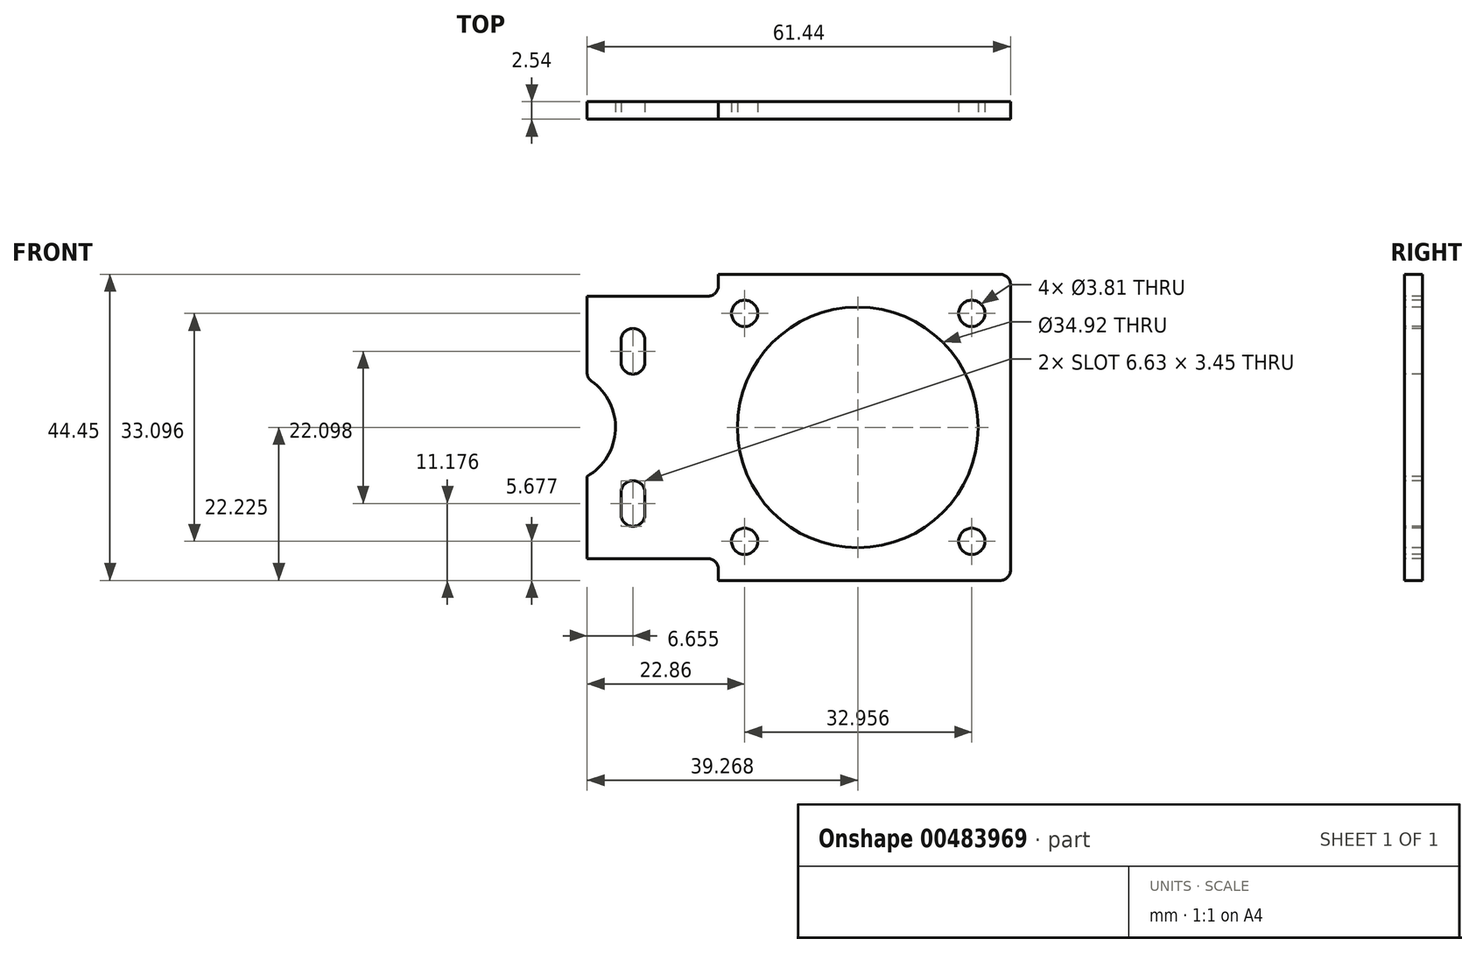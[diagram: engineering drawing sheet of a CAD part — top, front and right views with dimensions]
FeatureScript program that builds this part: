
annotation { "Feature Type Name" : "Feature", "Feature Type Description" : "" }
export const myFeature = defineFeature(function(context is Context, id is Id, definition is map)
    precondition{}
    {
        {
            var Q0;
            Q0=qCreatedBy(makeId("Top.planeOp"),FACE);
            var sketch = newSketch(context, id + "F0", { "sketchPlane" : qUnion([Q0])});
            skLineSegment(sketch, "E0.bottom", {"start": v(0, 0) * mm, "end": v(-30.48, 0) * mm});
            skLineSegment(sketch, "E0.top", {"start": v(0, 2.54) * mm, "end": v(-30.48, 2.54) * mm});
            skLineSegment(sketch, "E0.left", {"start": v(0, 0) * mm, "end": v(0, 2.54) * mm});
            skLineSegment(sketch, "E0.right", {"start": v(-30.48, 0) * mm, "end": v(-30.48, 2.54) * mm});
            skLineSegment(sketch, "E1", {"start": v(0, 2.54) * mm, "end": v(30.96, 2.54) * mm});
            skLineSegment(sketch, "E2", {"start": v(30.96, 2.54) * mm, "end": v(30.96, 0) * mm});
            skLineSegment(sketch, "E3", {"start": v(30.96, 0) * mm, "end": v(0, 0) * mm});
            skSolve(sketch);
        }
        {
            var Q0;
            Q0=makeQuery(id+"F0.imprint","IMPRINT",FACE,{"disambiguationData":[TD([[makeQuery(id+"F0.imprint","IMPRINT",EDGE,{"derivedFrom":sQuery(id+"F0.wireOp",EDGE,"E0.bottom")}),-1.0]])]});
            extrude(context, id + "F1", {"entities" : qUnion([Q0]), "depth" : 44.45 * mm});
        }
        {
            var Q0;
            Q0=makeQuery(id+"F1.opExtrude","SWEPT_FACE",FACE,{"disambiguationData":[OSD([sQuery(id+"F0.wireOp",EDGE,"E0.bottom")])]});
            var sketch = newSketch(context, id + "F2", { "sketchPlane" : qUnion([Q0])});
            skLineSegment(sketch, "E4", {"start": v(-30.48, 22.23) * mm, "end": v(-26.37, 22.23) * mm, "construction": true});
            skPoint(sketch, "E5", {"position": v(-30.48, 29.34) * mm});
            skPoint(sketch, "E6", {"position": v(-30.48, 15.11) * mm});
            skArc(sketch, "E7", {"start": v(-30.48, 15.11) * mm, "mid": v(-26.37, 22.23) * mm, "end": v(-30.48, 29.34) * mm});
            skLineSegment(sketch, "E8", {"start": v(-26.37, 22.23) * mm, "end": v(-23.83, 22.23) * mm, "construction": true});
            skLineSegment(sketch, "E9", {"start": v(-23.83, 33.27) * mm, "end": v(-23.83, 12.76) * mm, "construction": true});
            skLineSegment(sketch, "E10", {"start": v(-23.83, 33.27) * mm, "end": v(-23.83, 34.86) * mm, "construction": true});
            skLineSegment(sketch, "E11", {"start": v(-23.83, 11.18) * mm, "end": v(-23.83, 9.59) * mm, "construction": true});
            skLineSegment(sketch, "E12", {"start": v(-23.83, 33.27) * mm, "end": v(-23.83, 31.69) * mm, "construction": true});
            skArc(sketch, "E13", {"start": v(-22.1, 34.86) * mm, "mid": v(-23.83, 36.59) * mm, "end": v(-25.55, 34.86) * mm});
            skArc(sketch, "E14", {"start": v(-25.55, 31.69) * mm, "mid": v(-23.83, 29.96) * mm, "end": v(-22.1, 31.69) * mm});
            skArc(sketch, "E15", {"start": v(-22.1, 12.76) * mm, "mid": v(-23.83, 14.5) * mm, "end": v(-25.55, 12.76) * mm});
            skArc(sketch, "E16", {"start": v(-25.55, 9.59) * mm, "mid": v(-23.83, 7.86) * mm, "end": v(-22.1, 9.59) * mm});
            skLineSegment(sketch, "E17", {"start": v(-25.55, 12.76) * mm, "end": v(-25.55, 9.59) * mm});
            skLineSegment(sketch, "E18", {"start": v(-22.1, 12.76) * mm, "end": v(-22.1, 9.59) * mm});
            skLineSegment(sketch, "E19", {"start": v(-25.55, 34.86) * mm, "end": v(-25.55, 31.69) * mm});
            skLineSegment(sketch, "E20", {"start": v(-22.1, 34.86) * mm, "end": v(-22.1, 31.69) * mm});
            skLineSegment(sketch, "E21.trimOffspring", {"start": v(-23.83, 11.18) * mm, "end": v(-23.83, 12.76) * mm, "construction": true});
            skLineSegment(sketch, "E22.bottom", {"start": v(-30.48, 3.17) * mm, "end": v(-11.43, 3.17) * mm});
            skLineSegment(sketch, "E22.top", {"start": v(-30.48, 0) * mm, "end": v(-11.43, 0) * mm});
            skLineSegment(sketch, "E22.left", {"start": v(-30.48, 3.17) * mm, "end": v(-30.48, 0) * mm});
            skLineSegment(sketch, "E22.right", {"start": v(-11.43, 3.17) * mm, "end": v(-11.43, 0) * mm});
            skLineSegment(sketch, "E23.bottom", {"start": v(-30.48, 44.45) * mm, "end": v(-11.43, 44.45) * mm});
            skLineSegment(sketch, "E23.top", {"start": v(-30.48, 41.28) * mm, "end": v(-11.43, 41.28) * mm});
            skLineSegment(sketch, "E23.left", {"start": v(-30.48, 44.45) * mm, "end": v(-30.48, 41.28) * mm});
            skLineSegment(sketch, "E23.right", {"start": v(-11.43, 44.45) * mm, "end": v(-11.43, 41.28) * mm});
            skLineSegment(sketch, "E24", {"start": v(-11.43, 41.28) * mm, "end": v(-11.43, 3.17) * mm, "construction": true});
            skSolve(sketch);
        }
        {
            var Q0;
            Q0=makeQuery(id+"F0.imprint","IMPRINT",FACE,{"disambiguationData":[TD([[makeQuery(id+"F0.imprint","IMPRINT",EDGE,{"derivedFrom":sQuery(id+"F0.wireOp",EDGE,"E0.left")}),-1.0]])]});
            extrude(context, id + "F3", {"entities" : qUnion([Q0]), "operationType" : NewBodyOperationType.ADD, "depth" : 44.45 * mm});
        }
        {
            var Q0;
            Q0=makeQuery(id+"F3.boolean.opBoolean","MERGE",FACE,{"derivedFrom":[makeQuery(id+"F1.opExtrude","SWEPT_FACE",FACE,{"disambiguationData":[OSD([sQuery(id+"F0.wireOp",EDGE,"E0.bottom")])]}),makeQuery(id+"F3.opExtrude","SWEPT_FACE",FACE,{"disambiguationData":[OSD([sQuery(id+"F0.wireOp",EDGE,"E3")])]})]});
            var sketch = newSketch(context, id + "F4", { "sketchPlane" : qUnion([Q0])});
            skCircle(sketch, "E25", {"center": v(-7.62, 38.77) * mm, "radius": 1.9 * mm});
            skCircle(sketch, "E26", {"center": v(-7.62, 5.68) * mm, "radius": 1.9 * mm});
            skPoint(sketch, "E27", {"position": v(30.96, 5.68) * mm});
            skPoint(sketch, "E28", {"position": v(30.96, 38.77) * mm});
            skPoint(sketch, "E29", {"position": v(0, 22.23) * mm});
            skLineSegment(sketch, "E30", {"start": v(0, 0) * mm, "end": v(0, 44.45) * mm, "construction": true});
            skLineSegment(sketch, "E31", {"start": v(0, 22.23) * mm, "end": v(8.79, 22.23) * mm, "construction": true});
            skPoint(sketch, "E32", {"position": v(30.96, 34.36) * mm});
            skPoint(sketch, "E33", {"position": v(30.96, 5.09) * mm});
            skCircle(sketch, "E34", {"center": v(8.79, 22.23) * mm, "radius": 17.46 * mm});
            skLineSegment(sketch, "E35", {"start": v(-11.79, 44.45) * mm, "end": v(-11.79, 0) * mm, "construction": true});
            skLineSegment(sketch, "E36", {"start": v(-7.62, 38.77) * mm, "end": v(25.34, 38.77) * mm, "construction": true});
            skLineSegment(sketch, "E37", {"start": v(25.34, 38.77) * mm, "end": v(25.34, 5.68) * mm, "construction": true});
            skLineSegment(sketch, "E38", {"start": v(25.34, 5.68) * mm, "end": v(-7.62, 5.68) * mm, "construction": true});
            skLineSegment(sketch, "E39", {"start": v(5.98, 39.69) * mm, "end": v(12.26, 39.69) * mm, "construction": true});
            skLineSegment(sketch, "E40", {"start": v(26.25, 25.32) * mm, "end": v(26.25, 19.37) * mm, "construction": true});
            skCircle(sketch, "E41", {"center": v(25.34, 38.77) * mm, "radius": 1.9 * mm});
            skCircle(sketch, "E42", {"center": v(25.34, 5.68) * mm, "radius": 1.9 * mm});
            skPoint(sketch, "E43", {"position": v(21.92, 0) * mm});
            skSolve(sketch);
        }
        {
            var Q0;
            {var subQ0=sQuery(id+"F4.wireOp",EDGE,"oErodHu0-SVqe-cXD9-A2Iy-klHVv3QFz86o");Q0=makeQuery(id+"F4.imprint","IMPRINT",FACE,{"disambiguationData":[TD([[makeQuery(id+"F4.imprint","IMPRINT",EDGE,{"derivedFrom":subQ0}),1.0]])]});}
            var Q1;
            Q1=makeQuery(id+"F4.imprint","IMPRINT",FACE,{"disambiguationData":[TD([[makeQuery(id+"F4.imprint","IMPRINT",EDGE,{"derivedFrom":sQuery(id+"F4.wireOp",EDGE,"E25")}),1.0]])]});
            var Q2;
            Q2=makeQuery(id+"F4.imprint","IMPRINT",FACE,{"disambiguationData":[TD([[makeQuery(id+"F4.imprint","IMPRINT",EDGE,{"derivedFrom":sQuery(id+"F4.wireOp",EDGE,"E26")}),1.0]])]});
            var Q3;
            Q3=makeQuery(id+"F2.imprint","IMPRINT",FACE,{"disambiguationData":[TD([[makeQuery(id+"F2.imprint","IMPRINT",EDGE,{"derivedFrom":sQuery(id+"F2.wireOp",EDGE,"E15")}),1.0]])]});
            var Q4;
            Q4=makeQuery(id+"F2.imprint","IMPRINT",FACE,{"disambiguationData":[TD([[makeQuery(id+"F2.imprint","IMPRINT",EDGE,{"derivedFrom":sQuery(id+"F2.wireOp",EDGE,"E13")}),1.0]])]});
            var Q5;
            {var subQ0=sQuery(id+"F2.wireOp",EDGE,"E7");Q5=makeQuery(id+"F2.imprint","IMPRINT",FACE,{"disambiguationData":[TD([[makeQuery(id+"F2.imprint","IMPRINT",EDGE,{"derivedFrom":subQ0}),1.0]])]});}
            var Q6;
            {var subQ0=sQuery(id+"F4.wireOp",EDGE,"mWe7BF5G-u2iA-ggOj-CAzd-YLydOq5GdBwD");Q6=makeQuery(id+"F4.imprint","IMPRINT",FACE,{"disambiguationData":[TD([[makeQuery(id+"F4.imprint","IMPRINT",EDGE,{"derivedFrom":subQ0}),1.0]])]});}
            var Q7;
            Q7=makeQuery(id+"F4.imprint","IMPRINT",FACE,{"disambiguationData":[TD([[makeQuery(id+"F4.imprint","IMPRINT",EDGE,{"derivedFrom":sQuery(id+"F4.wireOp",EDGE,"E41")}),1.0]])]});
            var Q8;
            Q8=makeQuery(id+"F4.imprint","IMPRINT",FACE,{"disambiguationData":[TD([[makeQuery(id+"F4.imprint","IMPRINT",EDGE,{"derivedFrom":sQuery(id+"F4.wireOp",EDGE,"E42")}),1.0]])]});
            var Q9;
            Q9=makeQuery(id+"F4.imprint","IMPRINT",FACE,{"disambiguationData":[TD([[makeQuery(id+"F4.imprint","IMPRINT",EDGE,{"derivedFrom":sQuery(id+"F4.wireOp",EDGE,"E34")}),1.0]])]});
            extrude(context, id + "F5", {"entities" : qUnion([Q0, Q1, Q2, Q3, Q4, Q5, Q6, Q7, Q8, Q9]), "operationType" : NewBodyOperationType.REMOVE, "oppositeDirection" : true, "depth" : 25.4 * mm});
        }
        {
            var Q0;
            Q0=makeQuery(id+"F2.imprint","IMPRINT",FACE,{"disambiguationData":[TD([[makeQuery(id+"F2.imprint","IMPRINT",EDGE,{"derivedFrom":sQuery(id+"F2.wireOp",EDGE,"E23.bottom")}),1.0]])]});
            var Q1;
            Q1=makeQuery(id+"F2.imprint","IMPRINT",FACE,{"disambiguationData":[TD([[makeQuery(id+"F2.imprint","IMPRINT",EDGE,{"derivedFrom":sQuery(id+"F2.wireOp",EDGE,"E22.bottom")}),-1.0]])]});
            extrude(context, id + "F6", {"entities" : qUnion([Q0, Q1]), "operationType" : NewBodyOperationType.REMOVE, "oppositeDirection" : true, "depth" : 25.4 * mm});
        }
        {
            var Q0;
            Q0=makeQuery(id+"F6.boolean.opBoolean","COPY",EDGE,{"derivedFrom":makeQuery(id+"F6.opExtrude","SWEPT_EDGE",EDGE,{"disambiguationData":[OSD([sQuery(id+"F2.wireOp",EDGE,"E23.top"),sQuery(id+"F2.wireOp",EDGE,"E23.right")])]})});
            var Q1;
            Q1=makeQuery(id+"F6.boolean.opBoolean","COPY",EDGE,{"derivedFrom":makeQuery(id+"F6.opExtrude","SWEPT_EDGE",EDGE,{"disambiguationData":[OSD([sQuery(id+"F0.wireOp",EDGE,"E0.bottom"),sQuery(id+"F2.wireOp",EDGE,"E23.bottom"),sQuery(id+"F2.wireOp",EDGE,"E23.right")])]})});
            var Q2;
            Q2=makeQuery(id+"F6.boolean.opBoolean","COPY",EDGE,{"derivedFrom":makeQuery(id+"F6.opExtrude","SWEPT_EDGE",EDGE,{"disambiguationData":[OSD([sQuery(id+"F0.wireOp",EDGE,"E0.bottom"),sQuery(id+"F2.wireOp",EDGE,"E22.top"),sQuery(id+"F2.wireOp",EDGE,"E22.right")])]})});
            var Q3;
            Q3=makeQuery(id+"F6.boolean.opBoolean","COPY",EDGE,{"derivedFrom":makeQuery(id+"F6.opExtrude","SWEPT_EDGE",EDGE,{"disambiguationData":[OSD([sQuery(id+"F2.wireOp",EDGE,"E22.bottom"),sQuery(id+"F2.wireOp",EDGE,"E22.right")])]})});
            var Q4;
            Q4=makeQuery(id+"F6.boolean.opBoolean","COPY",EDGE,{"derivedFrom":makeQuery(id+"F6.opExtrude","SWEPT_EDGE",EDGE,{"disambiguationData":[OSD([sQuery(id+"F0.wireOp",EDGE,"E0.bottom"),sQuery(id+"F0.wireOp",EDGE,"E0.right"),sQuery(id+"F2.wireOp",EDGE,"E22.bottom"),sQuery(id+"F2.wireOp",EDGE,"E22.left")])]})});
            var Q5;
            {var subQ0=sQuery(id+"F2.wireOp",EDGE,"E7");var subQ1=sQuery(id+"F0.wireOp",EDGE,"E0.right");var subQ2=sQuery(id+"F0.wireOp",EDGE,"E0.bottom");Q5=makeQuery(id+"F5.boolean.opBoolean","COPY",EDGE,{"derivedFrom":makeQuery(id+"F5.opExtrude","SWEPT_EDGE",EDGE,{"disambiguationData":[OSD([subQ2,subQ1,subQ0]),TDD([makeQuery(id+"F2.imprint","INTERSECT",VERTEX,{"disambiguationData":[OD(0.0)],"derivedFrom":[makeQuery(id+"F1.opExtrude","SWEPT_EDGE",EDGE,{"disambiguationData":[OSD([subQ2,subQ1])]}),subQ0]})])]})});}
            var Q6;
            {var subQ0=sQuery(id+"F2.wireOp",EDGE,"E7");var subQ1=sQuery(id+"F0.wireOp",EDGE,"E0.right");var subQ2=sQuery(id+"F0.wireOp",EDGE,"E0.bottom");Q6=makeQuery(id+"F5.boolean.opBoolean","COPY",EDGE,{"derivedFrom":makeQuery(id+"F5.opExtrude","SWEPT_EDGE",EDGE,{"disambiguationData":[OSD([subQ2,subQ1,subQ0]),TDD([makeQuery(id+"F2.imprint","INTERSECT",VERTEX,{"disambiguationData":[OD(1.0)],"derivedFrom":[makeQuery(id+"F1.opExtrude","SWEPT_EDGE",EDGE,{"disambiguationData":[OSD([subQ2,subQ1])]}),subQ0]})])]})});}
            var Q7;
            Q7=makeQuery(id+"F6.boolean.opBoolean","COPY",EDGE,{"derivedFrom":makeQuery(id+"F6.opExtrude","SWEPT_EDGE",EDGE,{"disambiguationData":[OSD([sQuery(id+"F0.wireOp",EDGE,"E0.bottom"),sQuery(id+"F0.wireOp",EDGE,"E0.right"),sQuery(id+"F2.wireOp",EDGE,"E23.top"),sQuery(id+"F2.wireOp",EDGE,"E23.left")])]})});
            var Q8;
            Q8=makeQuery(id+"F3.opExtrude","CAP_EDGE",EDGE,{"disambiguationData":[OSD([sQuery(id+"F0.wireOp",EDGE,"E2")])],"isStart":true});
            var Q9;
            Q9=makeQuery(id+"F3.opExtrude","CAP_EDGE",EDGE,{"disambiguationData":[OSD([sQuery(id+"F0.wireOp",EDGE,"E2")])],"isStart":false});
            fillet(context, id + "F7", {"entities" : qUnion([Q0, Q1, Q2, Q3, Q4, Q5, Q6, Q7, Q8, Q9]), "radius" : 1.52 * mm, "tangentPropagation" : true, "allowEdgeOverflow" : false});
        }
    });
